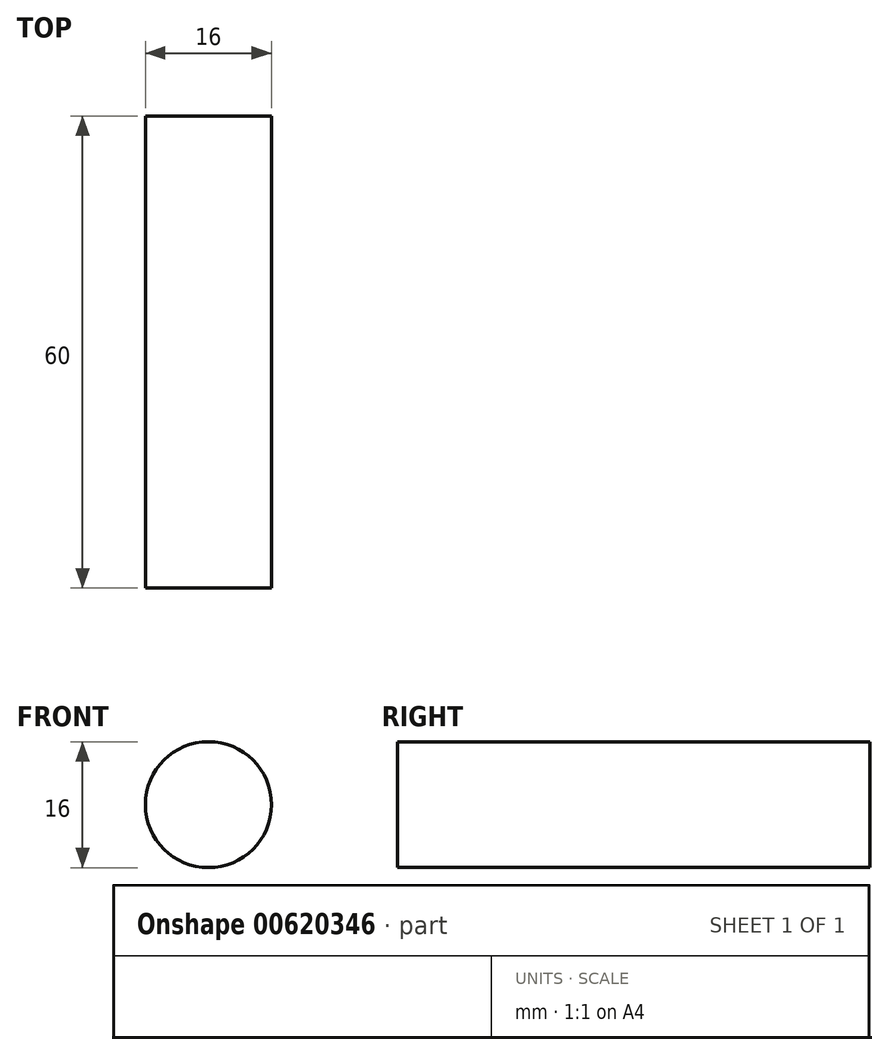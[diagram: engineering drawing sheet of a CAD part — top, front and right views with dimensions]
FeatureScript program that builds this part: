
annotation { "Feature Type Name" : "Feature", "Feature Type Description" : "" }
export const myFeature = defineFeature(function(context is Context, id is Id, definition is map)
    precondition{}
    {
        {
            var Q0;
            Q0=qCreatedBy(makeId("Front.planeOp"),FACE);
            var sketch = newSketch(context, id + "F0", { "sketchPlane" : qUnion([Q0])});
            skCircle(sketch, "E0", {"center": v(-16.08, 5.56) * mm, "radius": 8 * mm});
            skSolve(sketch);
        }
        {
            var Q0;
            Q0=makeQuery(id+"F0.imprint","IMPRINT",FACE,{"disambiguationData":[TD([[makeQuery(id+"F0.imprint","IMPRINT",EDGE,{"derivedFrom":sQuery(id+"F0.wireOp",EDGE,"E0")}),1.0]])]});
            extrude(context, id + "F1", {"entities" : qUnion([Q0]), "depth" : 60 * mm, "offsetDistance" : 25 * mm});
        }
    });
